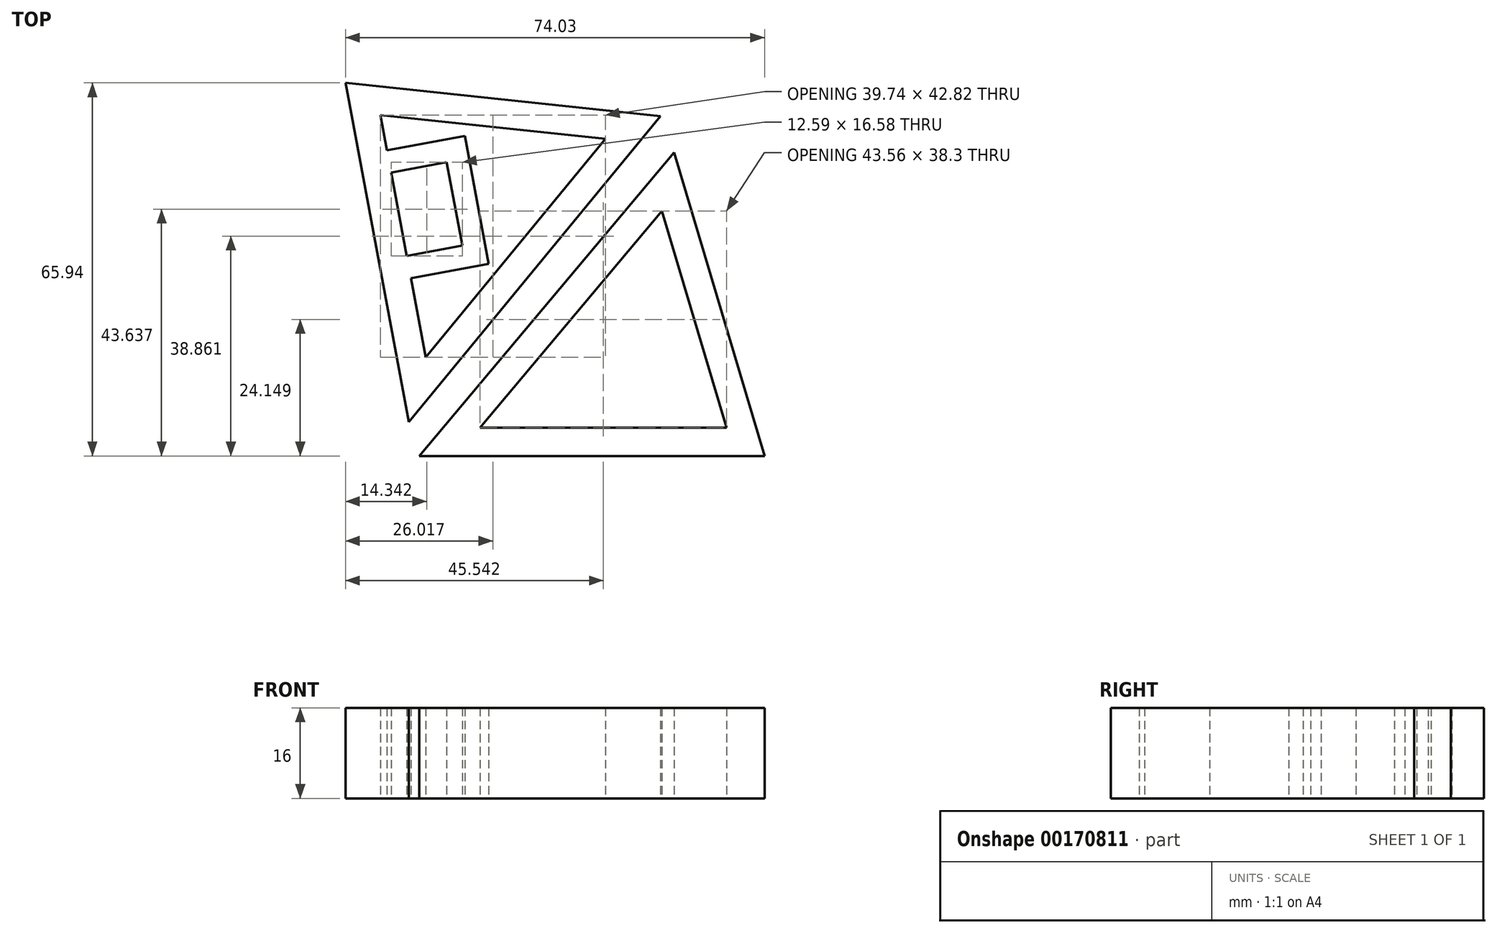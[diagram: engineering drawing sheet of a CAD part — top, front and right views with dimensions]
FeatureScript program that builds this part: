
annotation { "Feature Type Name" : "Feature", "Feature Type Description" : "" }
export const myFeature = defineFeature(function(context is Context, id is Id, definition is map)
    precondition{}
    {
        {
            var Q0;
            Q0=qCreatedBy(makeId("Top.planeOp"),FACE);
            var sketch = newSketch(context, id + "F0", { "sketchPlane" : qUnion([Q0])});
            skLineSegment(sketch, "E0", {"start": v(-10.1, 50.22) * mm, "end": v(42.6, 60.08) * mm, "construction": true});
            skLineSegment(sketch, "E1", {"start": v(42.6, 60.08) * mm, "end": v(-1.83, 6) * mm});
            skLineSegment(sketch, "E2", {"start": v(-1.83, 6) * mm, "end": v(-10.1, 50.22) * mm});
            skLineSegment(sketch, "E3", {"start": v(42.6, 60.08) * mm, "end": v(-13.04, 65.94) * mm});
            skLineSegment(sketch, "E4", {"start": v(-13.04, 65.94) * mm, "end": v(-10.1, 50.22) * mm});
            skLineSegment(sketch, "E5.1", {"start": v(32.85, 56.08) * mm, "end": v(1.11, 17.45) * mm});
            skLineSegment(sketch, "E5.2", {"start": v(32.85, 56.08) * mm, "end": v(-6.9, 60.27) * mm});
            skLineSegment(sketch, "E6", {"start": v(-5, 50.09) * mm, "end": v(4.84, 51.93) * mm});
            skLineSegment(sketch, "E7", {"start": v(4.84, 51.93) * mm, "end": v(7.6, 37.18) * mm});
            skLineSegment(sketch, "E8", {"start": v(7.6, 37.18) * mm, "end": v(-2.23, 35.35) * mm});
            skLineSegment(sketch, "E9.0", {"start": v(12.26, 33.99) * mm, "end": v(-1.5, 31.41) * mm});
            skLineSegment(sketch, "E9.1", {"start": v(8.03, 56.6) * mm, "end": v(12.26, 33.99) * mm});
            skLineSegment(sketch, "E9.2", {"start": v(-5.73, 54.02) * mm, "end": v(8.03, 56.6) * mm});
            skLineSegment(sketch, "E10.MirrorCS", {"start": v(0, 0) * mm, "end": v(45, 0) * mm});
            skLineSegment(sketch, "E11.MirrorCS", {"start": v(61, 0) * mm, "end": v(45, 0) * mm});
            skLineSegment(sketch, "E12.MirrorCS", {"start": v(45, 53.62) * mm, "end": v(61, 0) * mm});
            skLineSegment(sketch, "E13.MirrorCS", {"start": v(42.86, 43.3) * mm, "end": v(54.28, 5) * mm});
            skLineSegment(sketch, "E14.MirrorCS", {"start": v(45, 53.62) * mm, "end": v(0, 0) * mm});
            skLineSegment(sketch, "E15.MirrorCS", {"start": v(42.86, 43.3) * mm, "end": v(10.72, 5) * mm});
            skLineSegment(sketch, "E16.MirrorCS", {"start": v(45, 0) * mm, "end": v(45, 53.62) * mm, "construction": true});
            skLineSegment(sketch, "E17", {"start": v(-6.9, 60.27) * mm, "end": v(-5.73, 54.02) * mm});
            skLineSegment(sketch, "E18", {"start": v(-2.23, 35.35) * mm, "end": v(-5, 50.09) * mm});
            skLineSegment(sketch, "E19", {"start": v(-1.5, 31.41) * mm, "end": v(1.11, 17.45) * mm});
            skLineSegment(sketch, "E20", {"start": v(10.72, 5) * mm, "end": v(54.28, 5) * mm});
            skSolve(sketch);
        }
        {
            var Q0;
            Q0=makeQuery(id+"F0.imprint","IMPRINT",FACE,{"disambiguationData":[TD([[makeQuery(id+"F0.imprint","IMPRINT",EDGE,{"derivedFrom":sQuery(id+"F0.wireOp",EDGE,"E1")}),-1.0]])]});
            var Q1;
            {var subQ0=sQuery(id+"F0.wireOp",EDGE,"E6");Q1=makeQuery(id+"F0.imprint","IMPRINT",FACE,{"disambiguationData":[TD([[makeQuery(id+"F0.imprint","IMPRINT",EDGE,{"derivedFrom":subQ0}),1.0]])]});}
            var Q2;
            Q2=makeQuery(id+"F0.imprint","IMPRINT",FACE,{"disambiguationData":[TD([[makeQuery(id+"F0.imprint","IMPRINT",EDGE,{"derivedFrom":sQuery(id+"F0.wireOp",EDGE,"E10.MirrorCS")}),1.0]])]});
            extrude(context, id + "F1", {"entities" : qUnion([Q0, Q1, Q2]), "depth" : 16 * mm});
        }
    });
